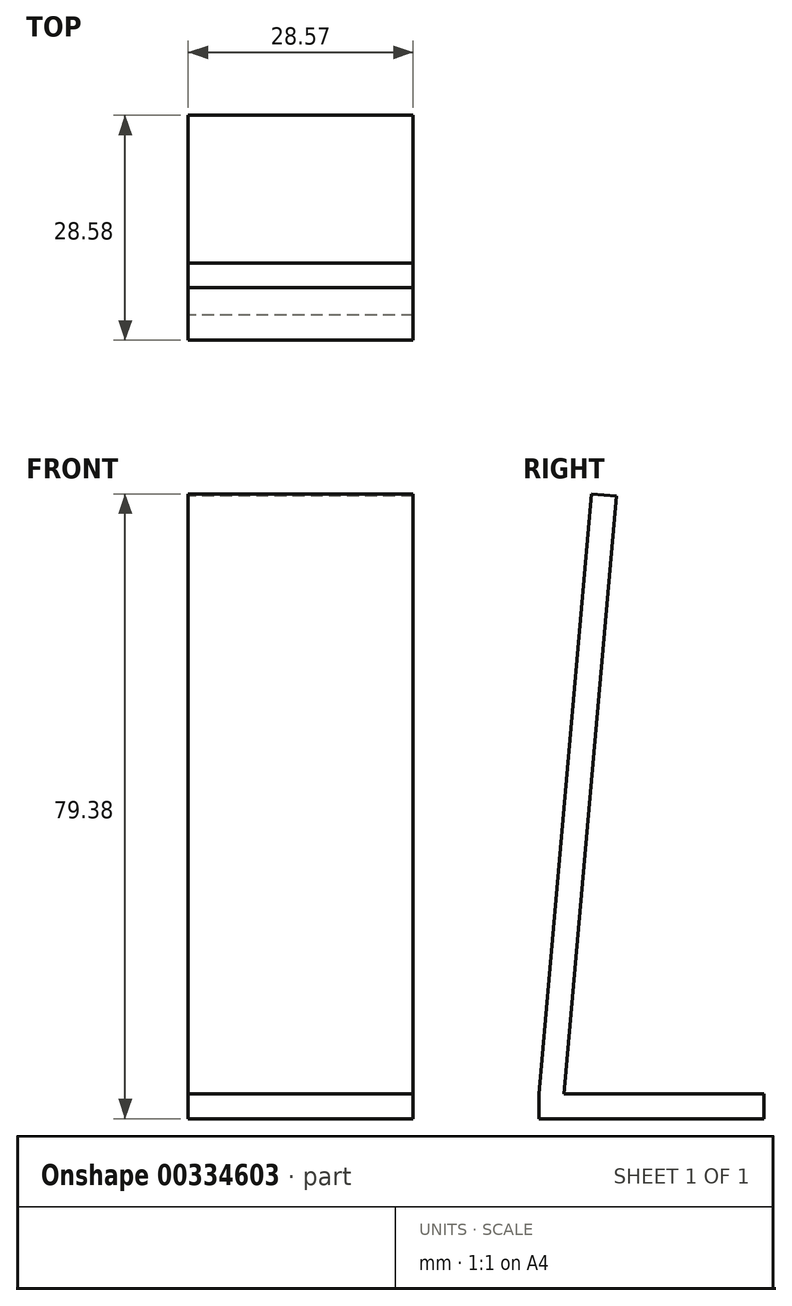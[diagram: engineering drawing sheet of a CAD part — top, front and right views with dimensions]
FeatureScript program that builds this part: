
annotation { "Feature Type Name" : "Feature", "Feature Type Description" : "" }
export const myFeature = defineFeature(function(context is Context, id is Id, definition is map)
    precondition{}
    {
        {
            var Q0;
            Q0=qCreatedBy(makeId("Right.planeOp"),FACE);
            var sketch = newSketch(context, id + "F0", { "sketchPlane" : qUnion([Q0])});
            skLineSegment(sketch, "E0", {"start": v(-14.29, 0) * mm, "end": v(14.29, 0) * mm});
            skLineSegment(sketch, "E1", {"start": v(14.29, 0) * mm, "end": v(14.29, 3.17) * mm});
            skLineSegment(sketch, "E2", {"start": v(14.29, 3.17) * mm, "end": v(-14.29, 3.17) * mm});
            skLineSegment(sketch, "E3", {"start": v(-14.29, 3.17) * mm, "end": v(-14.29, 0) * mm});
            skLineSegment(sketch, "E4", {"start": v(-5.01, 3.17) * mm, "end": v(-5.01, 79.38) * mm, "construction": true});
            skLineSegment(sketch, "E5", {"start": v(-14.29, 3.18) * mm, "end": v(-7.62, 79.37) * mm});
            skLineSegment(sketch, "E6", {"start": v(-7.62, 79.38) * mm, "end": v(-4.46, 79.1) * mm});
            skLineSegment(sketch, "E7", {"start": v(-4.46, 79.1) * mm, "end": v(-11.1, 3.18) * mm});
            skLineSegment(sketch, "E8", {"start": v(-11.1, 3.17) * mm, "end": v(-14.29, 3.17) * mm});
            skSolve(sketch);
        }
        {
            var Q0;
            Q0=qSketchRegion(id+"F0",true);
            extrude(context, id + "F1", {"entities" : qUnion([Q0]), "depth" : 28.57 * mm});
        }
    });
